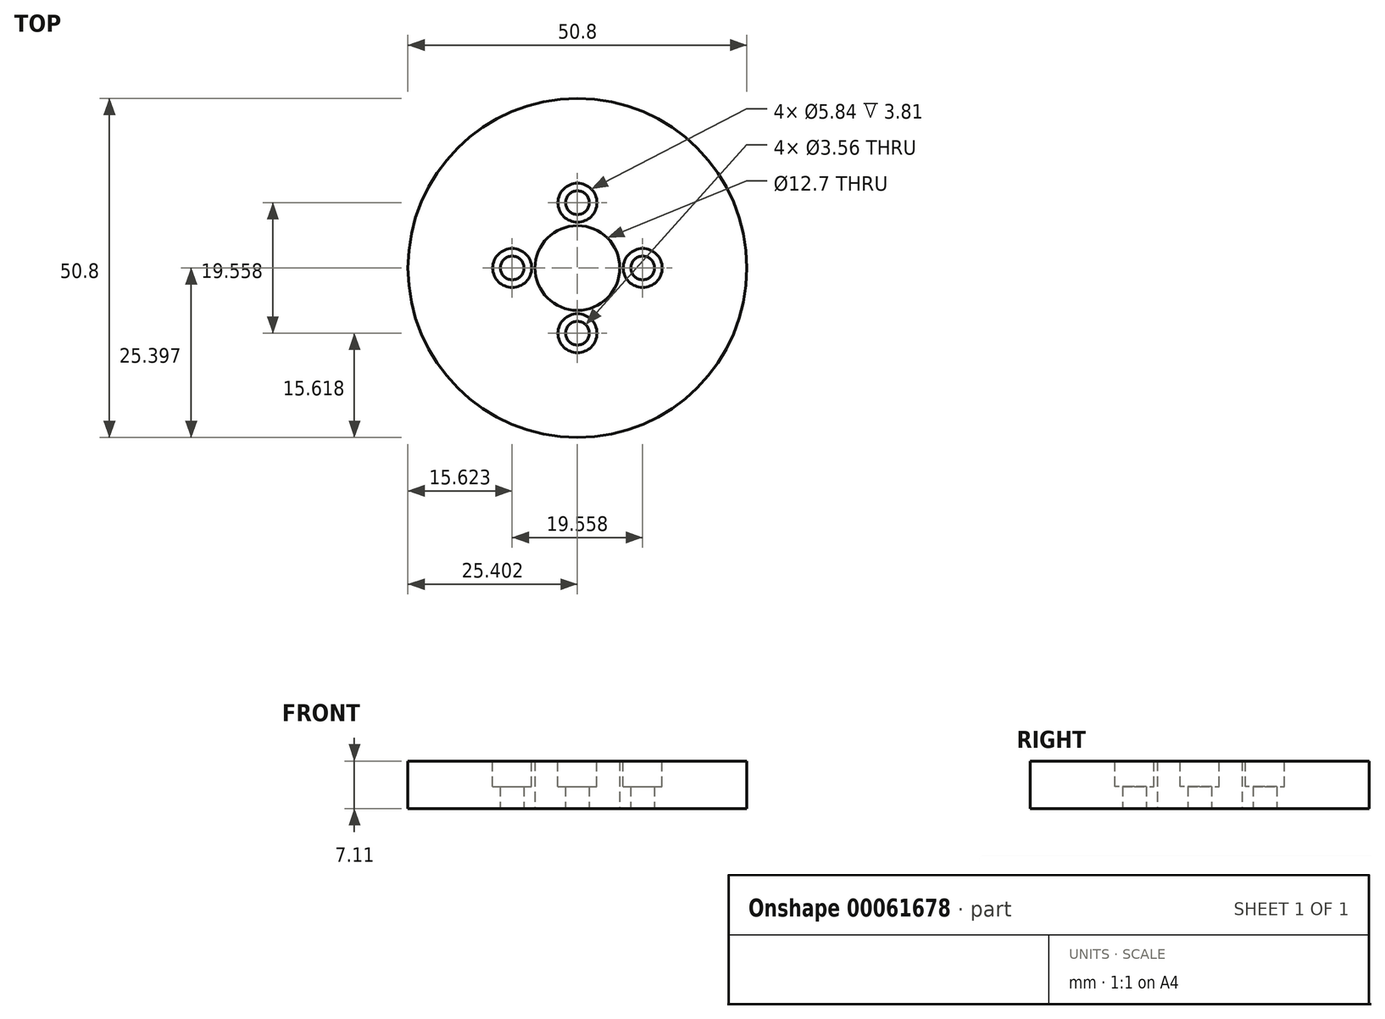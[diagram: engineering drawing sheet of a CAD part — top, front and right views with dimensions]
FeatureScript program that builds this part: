
annotation { "Feature Type Name" : "Feature", "Feature Type Description" : "" }
export const myFeature = defineFeature(function(context is Context, id is Id, definition is map)
    precondition{}
    {
        {
            var Q0;
            Q0=qCreatedBy(makeId("Top.planeOp"),FACE);
            var sketch = newSketch(context, id + "F0", { "sketchPlane" : qUnion([Q0])});
            skCircle(sketch, "E0", {"center": v(-1.89, 2.78) * mm, "radius": 25.4 * mm});
            skCircle(sketch, "E1", {"center": v(-1.89, 2.78) * mm, "radius": 6.35 * mm});
            skSolve(sketch);
        }
        {
            var Q0;
            Q0 = qSketchRegion(id + "F0", true);
            extrude(context, id + "F1", {"entities" : qUnion([Q0]), "depth" : 7.11 * mm});
        }
        {
            var Q0;
            Q0=makeQuery(id+"F1.opExtrude","CAP_FACE",FACE,{"disambiguationData":[OSD([sQuery(id+"F0.wireOp",EDGE,"E0"),sQuery(id+"F0.wireOp",EDGE,"E1")])],"isStart":false});
            var sketch = newSketch(context, id + "F2", { "sketchPlane" : qUnion([Q0])});
            skLineSegment(sketch, "E2", {"start": v(-1.89, 2.78) * mm, "end": v(-1.89, 12.56) * mm});
            skLineSegment(sketch, "E3", {"start": v(-1.89, 2.78) * mm, "end": v(-1.89, -7) * mm});
            skLineSegment(sketch, "E4", {"start": v(-1.89, 2.78) * mm, "end": v(-11.67, 2.78) * mm});
            skLineSegment(sketch, "E5", {"start": v(-1.89, 2.78) * mm, "end": v(7.9, 2.78) * mm});
            skCircle(sketch, "E6", {"center": v(-1.89, 12.56) * mm, "radius": 2.92 * mm});
            skCircle(sketch, "E7", {"center": v(-11.67, 2.78) * mm, "radius": 2.92 * mm});
            skCircle(sketch, "E8", {"center": v(7.9, 2.78) * mm, "radius": 2.92 * mm});
            skCircle(sketch, "E9", {"center": v(-1.89, -7) * mm, "radius": 2.92 * mm});
            skSolve(sketch);
        }
        {
            var Q0;
            Q0 = qSketchRegion(id + "F2", true);
            extrude(context, id + "F3", {"entities" : qUnion([Q0]), "operationType" : NewBodyOperationType.REMOVE, "oppositeDirection" : true, "depth" : 25.4 * mm});
        }
        {
            var Q0;
            Q0=makeQuery(id+"F1.opExtrude","CAP_FACE",FACE,{"disambiguationData":[OSD([sQuery(id+"F0.wireOp",EDGE,"E0"),sQuery(id+"F0.wireOp",EDGE,"E1")])],"isStart":true});
            var sketch = newSketch(context, id + "F4", { "sketchPlane" : qUnion([Q0])});
            skCircle(sketch, "E10", {"center": v(-1.89, 7) * mm, "radius": 1.78 * mm});
            skCircle(sketch, "E11", {"center": v(7.9, -2.78) * mm, "radius": 1.78 * mm});
            skCircle(sketch, "E12", {"center": v(-1.89, -12.56) * mm, "radius": 1.78 * mm});
            skCircle(sketch, "E13", {"center": v(-11.67, -2.78) * mm, "radius": 1.78 * mm});
            skCircle(sketch, "E14", {"center": v(-1.89, 7) * mm, "radius": 3.18 * mm});
            skCircle(sketch, "E15", {"center": v(7.9, -2.78) * mm, "radius": 3.15 * mm});
            skCircle(sketch, "E16", {"center": v(-1.89, -12.56) * mm, "radius": 3.16 * mm});
            skCircle(sketch, "E17", {"center": v(-11.67, -2.78) * mm, "radius": 3.1 * mm});
            skSolve(sketch);
        }
        {
            var Q0;
            Q0 = qSketchRegion(id + "F4", true);
            extrude(context, id + "F5", {"entities" : qUnion([Q0]), "operationType" : NewBodyOperationType.ADD, "oppositeDirection" : true, "depth" : 3.3 * mm});
        }
    });
